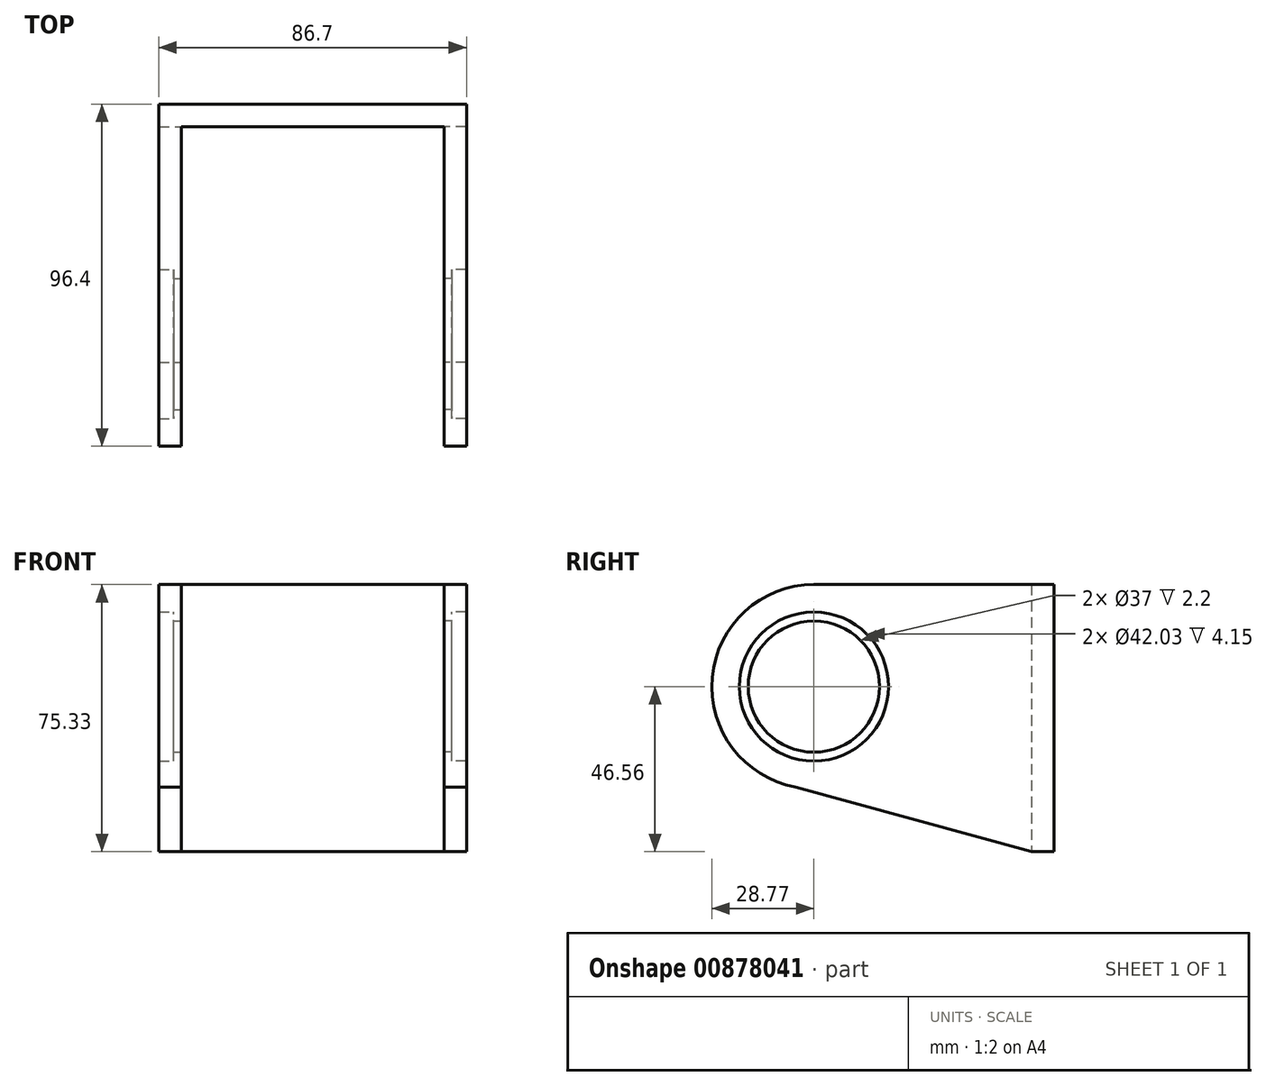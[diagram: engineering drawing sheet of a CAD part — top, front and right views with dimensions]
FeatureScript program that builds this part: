
annotation { "Feature Type Name" : "Feature", "Feature Type Description" : "" }
export const myFeature = defineFeature(function(context is Context, id is Id, definition is map)
    precondition{}
    {
        {
            var Q0;
            Q0=qCreatedBy(makeId("Right.planeOp"),FACE);
            var sketch = newSketch(context, id + "F0", { "sketchPlane" : qUnion([Q0])});
            skCircle(sketch, "E0", {"center": v(0, 0) * mm, "radius": 18.5 * mm});
            skCircle(sketch, "E1", {"center": v(0, 0) * mm, "radius": 23 * mm});
            skSolve(sketch);
        }
        {
            var Q0;
            Q0 = qSketchRegion(id + "F0", true);
            extrude(context, id + "F1", {"entities" : qUnion([Q0]), "depth" : 2.2 * mm, "offsetDistance" : 25 * mm});
        }
        {
            var Q0;
            Q0=qCreatedBy(makeId("Right.planeOp"),FACE);
            var sketch = newSketch(context, id + "F2", { "sketchPlane" : qUnion([Q0])});
            skCircle(sketch, "E2", {"center": v(0, 0) * mm, "radius": 28.77 * mm});
            skCircle(sketch, "E3", {"center": v(0, 0) * mm, "radius": 21.02 * mm});
            skSolve(sketch);
        }
        {
            var Q0;
            Q0=makeQuery(id+"F2.imprint","IMPRINT",FACE,{"disambiguationData":[TD([[makeQuery(id+"F2.imprint","IMPRINT",EDGE,{"derivedFrom":sQuery(id+"F2.wireOp",EDGE,"E2")}),1.0]])]});
            extrude(context, id + "F3", {"entities" : qUnion([Q0]), "operationType" : NewBodyOperationType.ADD, "depth" : 6.35 * mm, "offsetDistance" : 25 * mm});
        }
        {
            var Q0;
            Q0=qCreatedBy(makeId("Right.planeOp"),FACE);
            var sketch = newSketch(context, id + "F4", { "sketchPlane" : qUnion([Q0])});
            skLineSegment(sketch, "E4", {"start": v(0, 28.77) * mm, "end": v(61.28, 28.77) * mm});
            skLineSegment(sketch, "E5", {"start": v(61.28, 28.77) * mm, "end": v(61.28, -46.56) * mm});
            skLineSegment(sketch, "E6", {"start": v(61.28, -46.56) * mm, "end": v(-10.03, -26.96) * mm});
            skArc(sketch, "E7", {"start": v(-10.03, -26.96) * mm, "mid": v(28.31, -5.1) * mm, "end": v(0, 28.77) * mm});
            skSolve(sketch);
        }
        {
            var Q0;
            {var subQ0=sQuery(id+"F4.wireOp",EDGE,"E4");Q0=makeQuery(id+"F4.imprint","IMPRINT",FACE,{"disambiguationData":[TD([[makeQuery(id+"F4.imprint","IMPRINT",EDGE,{"derivedFrom":subQ0}),-1.0]])]});}
            extrude(context, id + "F5", {"entities" : qUnion([Q0]), "operationType" : NewBodyOperationType.ADD, "depth" : 6.35 * mm, "offsetDistance" : 25 * mm});
        }
        {
            var Q0;
            Q0=makeQuery(id+"F1.opExtrude","SWEPT_BODY",BODY,{"disambiguationData":[OSD([sQuery(id+"F0.wireOp",EDGE,"E0"),sQuery(id+"F0.wireOp",EDGE,"E1")])]});
            var Q1;
            Q1=qCreatedBy(makeId("Right.planeOp"),FACE);
            mirror(context, id + "F6", {"entities" : qUnion([Q0]), "mirrorPlane" : qUnion([Q1])});
        }
        {
            var Q0;
            Q0=makeQuery(id+"F6.opPattern","COPY",BODY,{"derivedFrom":makeQuery(id+"F1.opExtrude","SWEPT_BODY",BODY,{"disambiguationData":[OSD([sQuery(id+"F0.wireOp",EDGE,"E0"),sQuery(id+"F0.wireOp",EDGE,"E1")])]}),"instanceName":"1"});
            var Q1;
            Q1=qCreatedBy(makeId("Right.planeOp"),FACE);
            transform(context, id + "F7", {"entities" : qUnion([Q0]), "transformType" : TransformType.TRANSLATION_DISTANCE, "transformDirection" : qUnion([Q1]), "distance" : 74 * mm, "oppositeDirection" : true, "makeCopy" : false});
        }
        {
            var Q0;
            Q0=makeQuery(id+"F5.opExtrude","SWEPT_FACE",FACE,{"disambiguationData":[OSD([sQuery(id+"F4.wireOp",EDGE,"E5")])]});
            var sketch = newSketch(context, id + "F8", { "sketchPlane" : qUnion([Q0])});
            skLineSegment(sketch, "E8.bottom", {"start": v(-6.35, 28.77) * mm, "end": v(80.35, 28.77) * mm});
            skLineSegment(sketch, "E8.top", {"start": v(-6.35, -46.56) * mm, "end": v(80.35, -46.56) * mm});
            skLineSegment(sketch, "E8.left", {"start": v(-6.35, 28.77) * mm, "end": v(-6.35, -46.56) * mm});
            skLineSegment(sketch, "E8.right", {"start": v(80.35, 28.77) * mm, "end": v(80.35, -46.56) * mm});
            skSolve(sketch);
        }
        {
            var Q0;
            Q0 = qSketchRegion(id + "F8", true);
            extrude(context, id + "F9", {"entities" : qUnion([Q0]), "operationType" : NewBodyOperationType.ADD, "depth" : 6.35 * mm, "offsetDistance" : 25 * mm});
        }
    });
